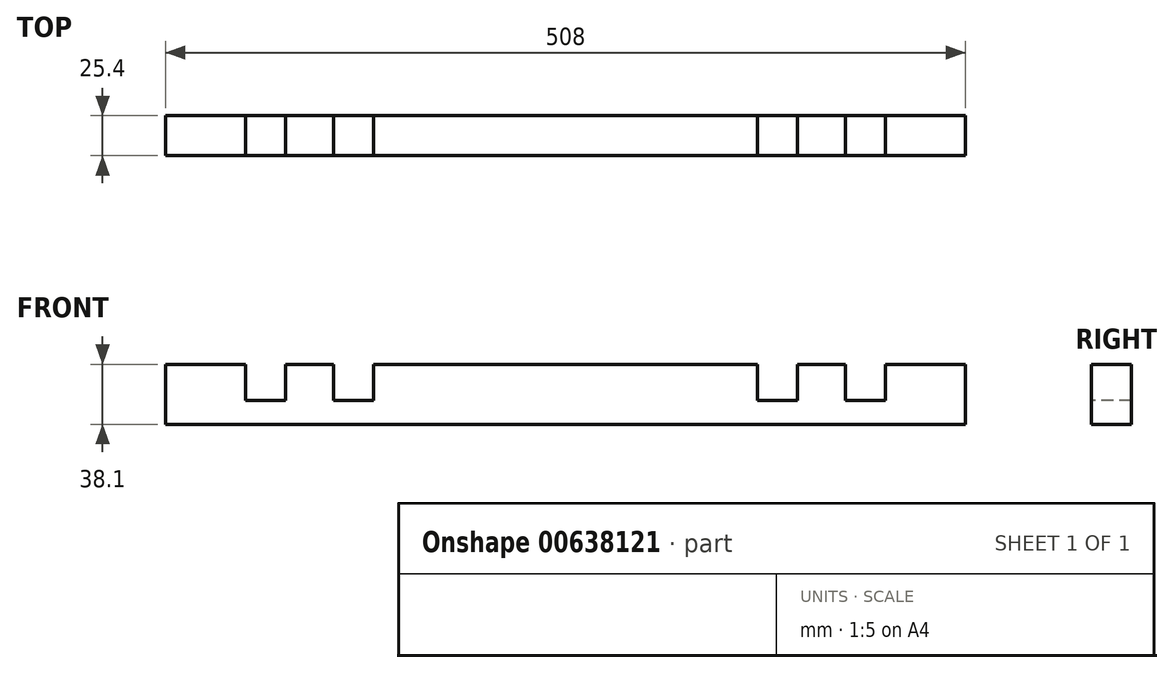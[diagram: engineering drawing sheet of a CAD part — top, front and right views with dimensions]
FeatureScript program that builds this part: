
annotation { "Feature Type Name" : "Feature", "Feature Type Description" : "" }
export const myFeature = defineFeature(function(context is Context, id is Id, definition is map)
    precondition{}
    {
        {
            var Q0;
            Q0=qCreatedBy(makeId("Front.planeOp"),FACE);
            var sketch = newSketch(context, id + "F0", { "sketchPlane" : qUnion([Q0])});
            skLineSegment(sketch, "E0", {"start": v(0, 0) * mm, "end": v(508, 0) * mm});
            skLineSegment(sketch, "E1", {"start": v(508, 0) * mm, "end": v(508, 38.1) * mm});
            skLineSegment(sketch, "E2", {"start": v(508, 38.1) * mm, "end": v(457.2, 38.1) * mm});
            skLineSegment(sketch, "E3", {"start": v(0, 38.1) * mm, "end": v(0, 0) * mm});
            skLineSegment(sketch, "E4", {"start": v(50.8, 38.1) * mm, "end": v(50.8, 15.24) * mm});
            skLineSegment(sketch, "E5", {"start": v(50.8, 15.24) * mm, "end": v(76.2, 15.24) * mm});
            skLineSegment(sketch, "E6", {"start": v(76.2, 15.24) * mm, "end": v(76.2, 38.1) * mm});
            skLineSegment(sketch, "E7", {"start": v(106.68, 38.1) * mm, "end": v(106.68, 15.24) * mm});
            skLineSegment(sketch, "E8", {"start": v(106.68, 15.24) * mm, "end": v(132.08, 15.24) * mm});
            skLineSegment(sketch, "E9", {"start": v(132.08, 15.24) * mm, "end": v(132.08, 38.1) * mm});
            skLineSegment(sketch, "E10.trimOffspring", {"start": v(50.8, 38.1) * mm, "end": v(0, 38.1) * mm});
            skLineSegment(sketch, "E11.trimOffspring", {"start": v(106.68, 38.1) * mm, "end": v(76.2, 38.1) * mm});
            skLineSegment(sketch, "E12", {"start": v(457.2, 38.1) * mm, "end": v(457.2, 15.24) * mm});
            skLineSegment(sketch, "E13", {"start": v(457.2, 15.24) * mm, "end": v(431.8, 15.24) * mm});
            skLineSegment(sketch, "E14", {"start": v(431.8, 15.24) * mm, "end": v(431.8, 38.1) * mm});
            skLineSegment(sketch, "E15.trimOffspring", {"start": v(431.8, 38.1) * mm, "end": v(401.32, 38.1) * mm});
            skLineSegment(sketch, "E16", {"start": v(401.32, 38.1) * mm, "end": v(401.32, 15.24) * mm});
            skLineSegment(sketch, "E17", {"start": v(401.32, 15.24) * mm, "end": v(375.92, 15.24) * mm});
            skLineSegment(sketch, "E18", {"start": v(375.92, 15.24) * mm, "end": v(375.92, 38.1) * mm});
            skLineSegment(sketch, "E19.trimOffspring", {"start": v(375.92, 38.1) * mm, "end": v(132.08, 38.1) * mm});
            skSolve(sketch);
        }
        {
            var Q0;
            Q0=makeQuery(id+"F0.imprint","IMPRINT",FACE,{"disambiguationData":[TD([[makeQuery(id+"F0.imprint","IMPRINT",EDGE,{"derivedFrom":sQuery(id+"F0.wireOp",EDGE,"E0")}),1.0]])]});
            extrude(context, id + "F1", {"entities" : qUnion([Q0]), "oppositeDirection" : true, "depth" : 25.4 * mm, "offsetDistance" : 25.4 * mm});
        }
    });
